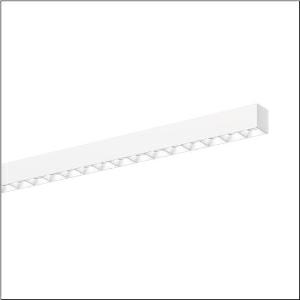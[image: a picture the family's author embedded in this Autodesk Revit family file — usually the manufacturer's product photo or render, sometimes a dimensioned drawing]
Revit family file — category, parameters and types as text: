
# Revit family: silica_r__21_51mx26da44wb_24d1
name_source: partatom
category: Lighting Fixtures
units: mm (PartAtom-declared; Revit-internal decimal feet)

## family parameters
Cut with Voids When Loaded = No
Host = Face
Light Source = No
Part Type = Normal
Room Calculation Point = No
Round Connector Dimension = Use Diameter
Shared = No

## types (1)
- --- (1 x LED, 4320 lm, 23.4 W, 4000K)
    Apparent Load = 23 VA
    CIE Flux Codes = 83 98 100 100 100
    Color Rendering = 80
    Color Temperature = 4000K
    Default Elevation = 1800 mm
    Description = Silica® 21, office luminaire, primary light control with darklight reflector, of PMMA, white, CAT 2 (L<= 3000cd/m²), light emission: direct distribution, primary light characteristic: symmetric, installation type: surface-mounted, LED, rated luminous flux: 4.320lm, luminous efficacy: 185lm/W, light colour: 840, colour temperature: 4000K, with terminal, 3+2-pole, max. 2.5mm², mains connection: 220..240V, AC, 50/60Hz, rated input power: 23.4W, luminaire housing, of aluminium, traffic white (RAL 9016), length: 1.204mm, width: 53mm, height: 53mm, protection rating (complete): IP20, insulation class (complete): insulation class I (protective earthing), certification: CE, permissible operating ambient temperature: 0..+35°C, standard: EN 50419, packaging unit: 1 piece
    Height = 0 mm  [stored 0 ft]
    Lamp = 1 x LED
    Lamp Light Flux = 4320 lm
    Lamp Power = 23.4 W
    Lamp count = 1
    Length = 1204 mm
    Luminous efficacy = 185 lm/W
    Manufacturer = Siteco
    ModVariant = No
    Model = 51MX26DA44WB
    Mounting Place = Ceiling
    Mounting Type = Recessed
    Number of Poles = 1
    OnlyDefault = Yes
    Power Factor = 1
    Product Name = Silica® 21
    Product group = office luminaire | ceiling recessed
    ProductGroupID = 401
    Protection Class = Protection class I
    Protection Degree = IP 20
    RLX_Detail_Level = 1
    RLX_Emergency_Light_Flux = 0 lm
    RLX_Emergency_Type = 0
    RLX_Emergency_Type_DB = No
    RlxData = <blob elided: 38621 chars, md5=8656afd8>
    Socket = socket
    Standby Power = 0 W
    System Light Flux = 4320 lm
    System Power = 23 W
    Type Comments = factory setting: luminous flux: 100 % | dim-lin: 254 | 337 mA
    Type Image = l_1313597.jpg
    URL = http://relux.com
    VarID = @adj_073651
    Voltage = 0 V
    Weight = 0.00 kg
    Width = 53 mm

note: [stored X ft] marks values corroborated as IEEE doubles in the binary element streams (Revit-internal decimal feet)

## geometry (parser evidence)
native form markers: Blend x4, Sweep x10
no freeform markers — native parametric forms only
